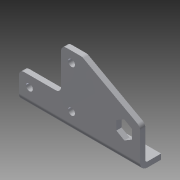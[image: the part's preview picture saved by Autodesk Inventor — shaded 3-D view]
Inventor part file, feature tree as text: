
AUTODESK INVENTOR PART (.ipt)
format: ipt  version: 2014 (Build 180170000, 170)  size: 134,656 bytes
history: native  units: in
note: dims shown in document units (in); Inventor stores cm internally (conversion verified against a paired STEP export)
features: sheet_metal_op x4, sketch x2, other x2, fillet x1
ambient origin geometry x8: Origin, YZ Plane, XZ Plane, XY Plane, X Axis, Y Axis, Z Axis, Center Point
bodies: Solid1 (feature_tree)
feature tree (9):
  sheet_metal_op  "Face1"
  sheet_metal_op  "Flange1"
  fillet  "Fillet2"  Radius=0.5in
  sketch  "Sketch1"  dims[d1=1.0in]
  other  "Plate1"
  sketch  "Sketch2"  dims[d2=1.0in d3=0.5in d4=2.875in d5=0.375in d6=0.5in d7=0.375in d8=90.0deg d9=0.75in d10=0.163in d11=0.25in d12=0.25in d13=0.7874in d15=1.0in d16=0.3937in d18=1.0in d20=0.7874in d22=1.0in d23=0.3937in d25=1.0in d27=0.125in d29=0.125in d30=0.0625in d31=0.25in d32=0.125in d33=0.5in d34=90.0deg d35=0.05in d36=0.5in d37=0.125in d38=0.125in d39=0.125in]
  other  "Plate2"
  sheet_metal_op  "Bend1"
  sheet_metal_op  "Corner1"
